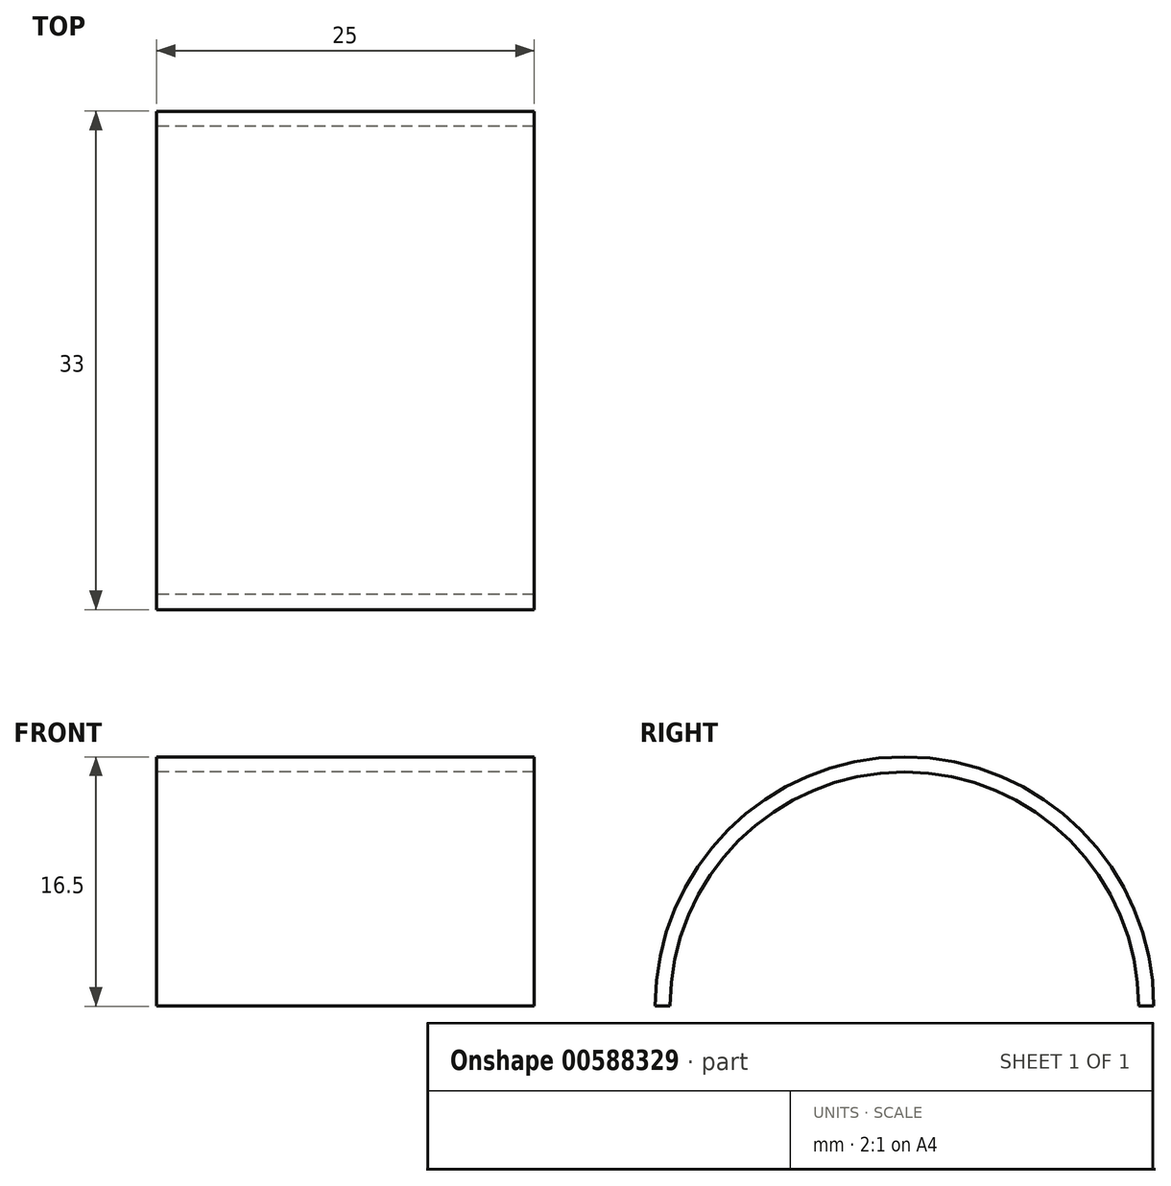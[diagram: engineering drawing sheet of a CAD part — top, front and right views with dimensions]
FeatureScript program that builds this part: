
annotation { "Feature Type Name" : "Feature", "Feature Type Description" : "" }
export const myFeature = defineFeature(function(context is Context, id is Id, definition is map)
    precondition{}
    {
        {
            var Q0;
            Q0=qCreatedBy(makeId("Right.planeOp"),FACE);
            var sketch = newSketch(context, id + "F0", { "sketchPlane" : qUnion([Q0])});
            skLineSegment(sketch, "E0", {"start": v(-18.96, -21.94) * mm, "end": v(-17.96, -21.94) * mm});
            skArc(sketch, "E1", {"start": v(13.04, -21.94) * mm, "mid": v(-2.46, -6.44) * mm, "end": v(-17.96, -21.94) * mm});
            skArc(sketch, "E2", {"start": v(14.04, -21.94) * mm, "mid": v(-2.46, -5.44) * mm, "end": v(-18.96, -21.94) * mm});
            skLineSegment(sketch, "E3.trimOffspring", {"start": v(13.04, -21.94) * mm, "end": v(14.04, -21.94) * mm});
            skPoint(sketch, "E4.orphan", {"position": v(-57.3, -21.94) * mm});
            skPoint(sketch, "E5.orphan", {"position": v(52.38, -21.94) * mm});
            skSolve(sketch);
        }
        {
            var Q0;
            Q0=makeQuery(id+"F0.imprint","IMPRINT",FACE,{"disambiguationData":[TD([[makeQuery(id+"F0.imprint","IMPRINT",EDGE,{"derivedFrom":sQuery(id+"F0.wireOp",EDGE,"E0")}),1.0]])]});
            extrude(context, id + "F1", {"entities" : qUnion([Q0]), "depth" : 25 * mm, "offsetDistance" : 25 * mm});
        }
    });
